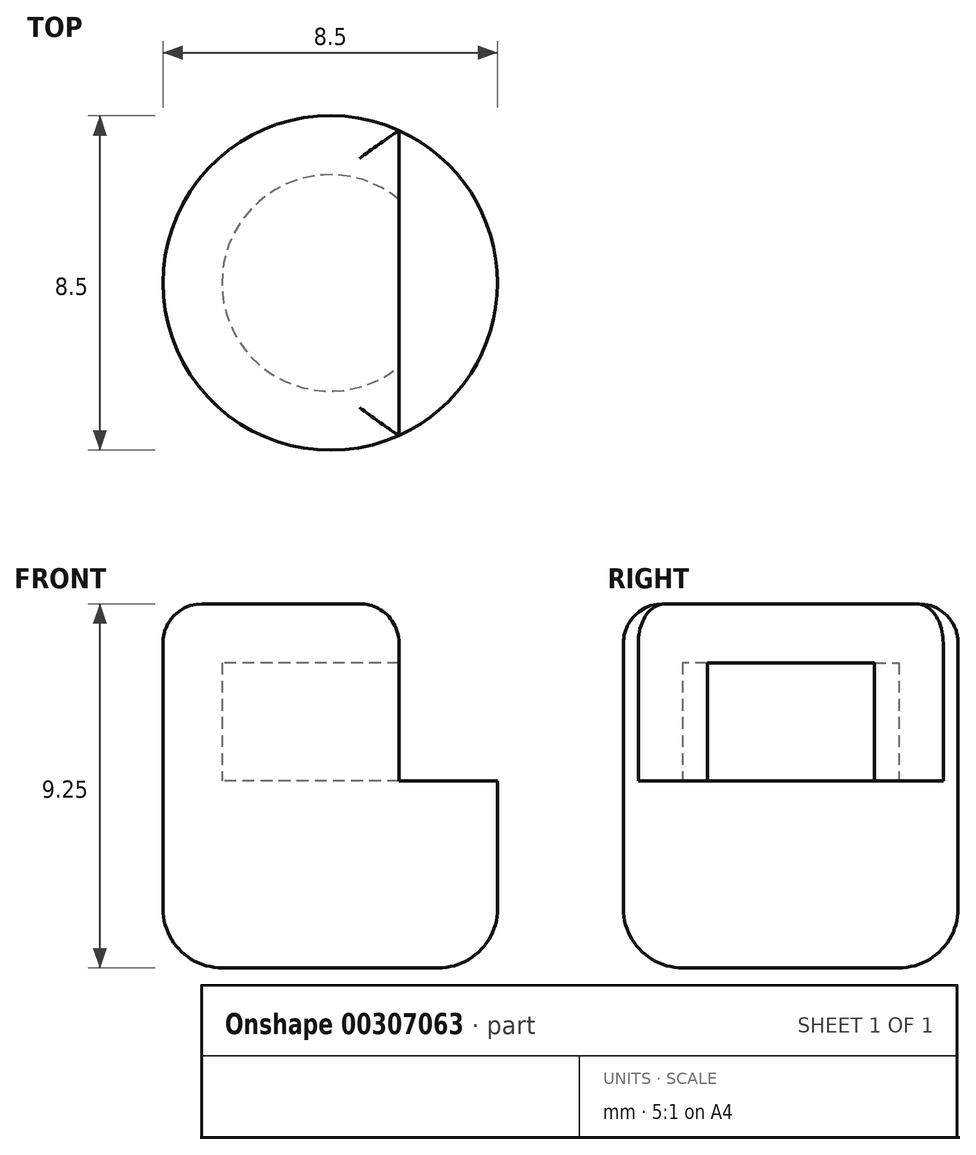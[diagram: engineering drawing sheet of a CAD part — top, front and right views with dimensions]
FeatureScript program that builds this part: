
annotation { "Feature Type Name" : "Feature", "Feature Type Description" : "" }
export const myFeature = defineFeature(function(context is Context, id is Id, definition is map)
    precondition{}
    {
        {
            var Q0;
            Q0=qCreatedBy(makeId("Top.planeOp"),FACE);
            var sketch = newSketch(context, id + "F0", { "sketchPlane" : qUnion([Q0])});
            skCircle(sketch, "E0", {"center": v(0, 0) * mm, "radius": 4.25 * mm});
            skSolve(sketch);
        }
        {
            var Q0;
            Q0 = qSketchRegion(id + "F0", true);
            extrude(context, id + "F1", {"entities" : qUnion([Q0]), "oppositeDirection" : true, "depth" : 4.75 * mm});
        }
        {
            var Q0;
            Q0=makeQuery(id+"F1.opExtrude","CAP_FACE",FACE,{"disambiguationData":[OSD([sQuery(id+"F0.wireOp",EDGE,"E0")])],"isStart":true});
            var sketch = newSketch(context, id + "F2", { "sketchPlane" : qUnion([Q0])});
            skCircle(sketch, "E1", {"center": v(0, 0) * mm, "radius": 2.75 * mm});
            skLineSegment(sketch, "E2", {"start": v(1.75, 3.87) * mm, "end": v(1.75, -3.87) * mm});
            skLineSegment(sketch, "E3", {"start": v(-4.25, 0) * mm, "end": v(1.75, 0) * mm});
            skSolve(sketch);
        }
        {
            var Q0;
            {var subQ0=sQuery(id+"F2.wireOp",EDGE,"E3");var subQ1=sQuery(id+"F2.wireOp",EDGE,"E1");var subQ2=makeQuery(id+"F2.imprint","INTERSECT",VERTEX,{"derivedFrom":[subQ1,subQ0]});Q0=makeQuery(id+"F2.imprint","IMPRINT",FACE,{"disambiguationData":[TD([[makeQuery(id+"F2.imprint","IMPRINT",EDGE,{"disambiguationData":[TD([[subQ2,1.0]])],"derivedFrom":subQ1}),-1.0]])]});}
            var Q1;
            {var subQ0=sQuery(id+"F2.wireOp",EDGE,"E3");var subQ1=sQuery(id+"F2.wireOp",EDGE,"E1");var subQ2=makeQuery(id+"F2.imprint","INTERSECT",VERTEX,{"derivedFrom":[subQ1,subQ0]});Q1=makeQuery(id+"F2.imprint","IMPRINT",FACE,{"disambiguationData":[TD([[makeQuery(id+"F2.imprint","IMPRINT",EDGE,{"disambiguationData":[TD([[subQ2,-1.0]])],"derivedFrom":subQ1}),-1.0]])]});}
            extrude(context, id + "F3", {"entities" : qUnion([Q0, Q1]), "operationType" : NewBodyOperationType.ADD, "depth" : 3 * mm});
        }
        {
            var Q0;
            Q0=makeQuery(id+"F3.opExtrude","CAP_FACE",FACE,{"disambiguationData":[OSD([sQuery(id+"F0.wireOp",EDGE,"E0"),sQuery(id+"F2.wireOp",EDGE,"E1"),sQuery(id+"F2.wireOp",EDGE,"E2")])],"isStart":false});
            var sketch = newSketch(context, id + "F4", { "sketchPlane" : qUnion([Q0])});
            skCircle(sketch, "E4", {"center": v(0, 0) * mm, "radius": 4.25 * mm});
            skLineSegment(sketch, "E5", {"start": v(1.75, 3.87) * mm, "end": v(1.75, -3.87) * mm});
            skSolve(sketch);
        }
        {
            var Q0;
            {var subQ4=makeQuery(id+"F3.opExtrude","CAP_EDGE",EDGE,{"disambiguationData":[OSD([sQuery(id+"F2.wireOp",EDGE,"E1")])],"isStart":false});Q0=makeQuery(id+"F4.imprint","IMPRINT",FACE,{"disambiguationData":[TD([[makeQuery(id+"F4.imprint","IMPRINT",EDGE,{"derivedFrom":subQ4}),-1.0]])]});}
            var Q1;
            {var subQ1=makeQuery(id+"F3.opExtrude","CAP_EDGE",EDGE,{"disambiguationData":[OSD([sQuery(id+"F2.wireOp",EDGE,"E1")])],"isStart":false});Q1=makeQuery(id+"F4.imprint","IMPRINT",FACE,{"disambiguationData":[TD([[makeQuery(id+"F4.imprint","IMPRINT",EDGE,{"derivedFrom":subQ1}),1.0]])]});}
            extrude(context, id + "F5", {"entities" : qUnion([Q0, Q1]), "operationType" : NewBodyOperationType.ADD, "depth" : 1.5 * mm});
        }
        {
            var Q0;
            Q0=makeQuery(id+"F1.opExtrude","CAP_EDGE",EDGE,{"disambiguationData":[OSD([sQuery(id+"F0.wireOp",EDGE,"E0")])],"isStart":false});
            fillet(context, id + "F6", {"entities" : qUnion([Q0]), "radius" : 1.5 * mm, "tangentPropagation" : true, "allowEdgeOverflow" : false});
        }
        {
            var Q0;
            Q0=makeQuery(id+"F5.opExtrude","CAP_EDGE",EDGE,{"disambiguationData":[OSD([sQuery(id+"F4.wireOp",EDGE,"E5")])],"isStart":false});
            var Q1;
            Q1=makeQuery(id+"F5.opExtrude","CAP_EDGE",EDGE,{"disambiguationData":[OSD([sQuery(id+"F4.wireOp",EDGE,"E4")])],"isStart":false});
            fillet(context, id + "F7", {"entities" : qUnion([Q0, Q1]), "radius" : 1 * mm, "tangentPropagation" : true, "allowEdgeOverflow" : false});
        }
    });
